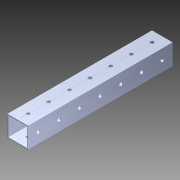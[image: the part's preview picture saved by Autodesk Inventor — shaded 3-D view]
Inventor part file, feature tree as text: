
AUTODESK INVENTOR PART (.ipt)
format: ipt  version: 2014 SP1 (Build 180222100, 222)  size: 1,102,336 bytes
history: native  units: in
note: dims shown in document units (in); Inventor stores cm internally (conversion verified against a paired STEP export)
features: pattern_circular x1, other x1, extrude x1, imported_body x1, sketch x1
ambient origin geometry x8: Origin, YZ Plane, XZ Plane, XY Plane, X Axis, Y Axis, Z Axis, Center Point
bodies: Body1 (feature_tree)
feature tree (5):
  pattern_circular  "CirPattern2"
  other  "1x1 tube1"
  extrude  "Extrusion1"  [1 undecoded]
  imported_body  "Base1"
  sketch  "Sketch1"  dims[d0=52.0in d1=0.0in]
note: 1 required parameter value undecoded (feature->parameter linkage not recoverable at this tier; creation-order binding heuristic only, values carry confidence <= 0.55)
